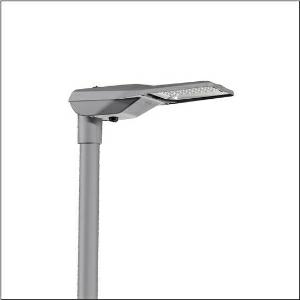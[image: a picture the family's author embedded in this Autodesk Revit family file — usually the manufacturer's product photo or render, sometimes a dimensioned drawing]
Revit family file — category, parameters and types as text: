
# Revit family: streetlight_sl_21_iq_mini___st1_0ab_5xe2m31y08jb_87eb
name_source: partatom
category: Lighting Fixtures
units: mm (PartAtom-declared; Revit-internal decimal feet)

## family parameters
Cut with Voids When Loaded = No
Host = Face
Light Source = No
Part Type = Normal
Room Calculation Point = No
Round Connector Dimension = Use Diameter
Shared = No

## types (1)
- --- (1 x LED, 9870 lm, 72.5 W, 3000K)
    Apparent Load = 73 VA
    CIE Flux Codes = 40 74 97 100 100
    Color Rendering = 70
    Color Temperature = 3000K
    Default Elevation = 1800 mm
    Description = Streetlight SL 21 iQ mini, mast luminaire, primary light control with lens, of PMMA, primary optical cover: cover, of toughened safety glass, transparent, light distribution: ST1.0aB, light emission: direct distribution, primary light characteristic: asymmetric, installation type: post-top, side-entry, LED, High Power LED, rated luminous flux: 9.870lm, luminous efficacy: 136lm/W, light colour: 730, colour temperature: 3000K, control gear: iQ-Street Remote, D4i with power reduction, control: pre-setting: logarithmic dimming characteristic, Street-Remote, Auto-Match, Temp-Guard, Lumen-Switch, Night-Set, Smart-Wire, Light-Fading, Desk-Remote (wireless, voltage-free reading and setting of iQ features in the workshop via application-optimized NFC function/RFID function), optimised constant luminous flux control (CLO 2.0), mains connection: 220..240V, AC, 50/60Hz, start of lifetime: 73W, end of service life: 76W, reduction: 33W, luminaire housing, of diecast aluminium, powder-coated, SITECO metallic grey (DB 702S), corrosivity category C5 high according to DIN EN ISO 12944, please order mast flange separately, inclination adjustable: 0°, 5°, 10°, 15°, sealing non-destructively replaceable, multi-level sealing system, length: 628mm, width: 235mm, height: 110mm, mast flange for spigot size: 42mm (side-entry): 5XC10008XM4, 60/48mm (side-entry/post-top): 5XC10108XM2, 76/60mm (side-entry/post-top): 5XC10108XM1, mounting height: 4..8m, Smart Interface below and above, protection rating (complete): IP66, insulation class (complete): insulation class II (safety insulation), certification: CE, ENEC, ENEC+, VDE, impact resistance: IK10, permissible operating ambient temperature for outdoor applications: -40..+50°C, standard-compliant lighting for roads and squares, packaging unit: 1 piece

Light Distribution: ST1.0aB
    Height = 110 mm
    Lamp = 1 x LED
    Lamp Light Flux = 9870 lm
    Lamp Power = 72.5 W
    Lamp count = 1
    Length = 625 mm
    Luminous efficacy = 136 lm/W
    Manufacturer = Siteco
    ModVariant = No
    Model = 5XE2M31Y08JB
    Number of Poles = 1
    OnlyDefault = Yes
    Power Factor = 1
    Product Name = Streetlight SL 21 iQ mini | ST1.0aB
    Product group = mast luminaire | pylon top
    ProductGroupID = 6100
    Protection Class = Protection class II
    Protection Degree = IP 66
    RLX_Detail_Level = 1
    RLX_Emergency_Light_Flux = 0 lm
    RLX_Emergency_Type = 0
    RLX_Emergency_Type_DB = No
    RlxData = <blob elided: 92809 chars, md5=248cc645>
    Socket = socket
    Standby Power = 0 W
    System Light Flux = 9870 lm
    System Power = 73 W
    Type Comments = factory setting: luminous flux: 100 % | dim-lin: 254 | 755 mA
    Type Image = l_1003514.jpg
    URL = http://relux.com
    VarID = @adj_112163
    Voltage = 0 V
    Weight = 0.00 kg
    Width = 234 mm

## geometry (parser evidence)
native form markers: Blend x4, Sweep x11
no freeform markers — native parametric forms only
